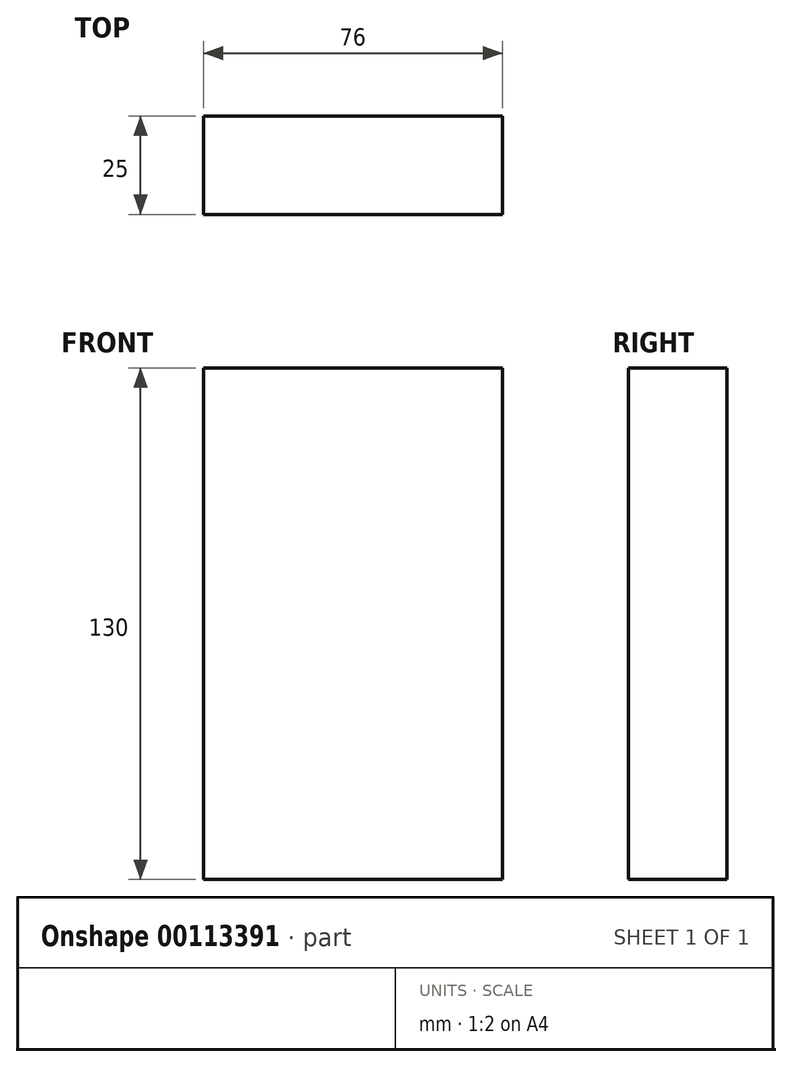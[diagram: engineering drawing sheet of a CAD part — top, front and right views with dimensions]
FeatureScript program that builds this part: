
annotation { "Feature Type Name" : "Feature", "Feature Type Description" : "" }
export const myFeature = defineFeature(function(context is Context, id is Id, definition is map)
    precondition{}
    {
        {
            var Q0;
            Q0=qCreatedBy(makeId("Front.planeOp"),FACE);
            var sketch = newSketch(context, id + "F0", { "sketchPlane" : qUnion([Q0])});
            skLineSegment(sketch, "E0", {"start": v(0, 0) * mm, "end": v(0, 130) * mm});
            skLineSegment(sketch, "E1", {"start": v(0, 130) * mm, "end": v(76, 130) * mm});
            skLineSegment(sketch, "E2", {"start": v(76, 130) * mm, "end": v(76, 0) * mm});
            skLineSegment(sketch, "E3", {"start": v(76, 0) * mm, "end": v(0, 0) * mm});
            skSolve(sketch);
        }
        {
            var Q0;
            Q0=makeQuery(id+"F0.imprint","IMPRINT",FACE,{"disambiguationData":[TD([[makeQuery(id+"F0.imprint","IMPRINT",EDGE,{"derivedFrom":sQuery(id+"F0.wireOp",EDGE,"E0")}),-1.0]])]});
            extrude(context, id + "F1", {"entities" : qUnion([Q0]), "depth" : 25 * mm});
        }
    });
